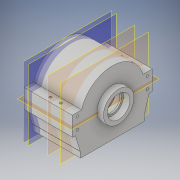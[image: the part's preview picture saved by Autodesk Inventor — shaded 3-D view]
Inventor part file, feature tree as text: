
AUTODESK INVENTOR PART (.ipt)
format: ipt  version: 2019 (Build 230136000, 136)  size: 587,776 bytes
history: native  units: mm
features: sketch x28, extrude x21, mirror x13, plane x12, projected_geometry x11, fillet x4, hole x3, other x1
ambient origin geometry x8: Origin, YZ Plane, XZ Plane, XY Plane, X Axis, Y Axis, Z Axis, Center Point
bodies: Body1 (feature_tree)
feature tree (93):
  other  "實體1"
  extrude  "擠出1"  Depth=123.43mm
  plane  "工作平面2"
  extrude  "擠出3"  Depth=160.0mm
  plane  "工作平面3"
  sketch  "草圖5"
  extrude  "擠出4"  Depth=120.0mm TaperAngle=0.0deg
  extrude  "擠出5"  [1 undecoded]
  plane  "工作平面4"
  extrude  "擠出7"  Depth=130.0mm
  plane  "工作平面5"
  extrude  "擠出9"  Depth=15.0mm TaperAngle=0.0deg
  extrude  "擠出10"  [1 undecoded]
  extrude  "擠出11"  Depth=140.0mm
  extrude  "擠出12"  Depth=10.0mm TaperAngle=0.0deg
  mirror  "鏡射1"
  fillet  "圓角2"  Radius=10.0mm
  fillet  "圓角3"  Radius=10.0mm
  sketch  "草圖16"
  plane  "工作平面7"
  mirror  "鏡射2"
  fillet  "圓角5"  [1 undecoded]
  fillet  "圓角6"  Radius=10.0mm
  plane  "工作平面8"
  plane  "工作平面9"
  sketch  "草圖20"
  sketch  "草圖21"
  extrude  "擠出15"  [1 undecoded]
  plane  "工作平面10"
  extrude  "擠出16"  Depth=10.0mm
  extrude  "擠出17"  Depth=10.0mm TaperAngle=0.0deg
  plane  "工作平面11"
  extrude  "擠出19"  Depth=10.0mm TaperAngle=0.0deg
  extrude  "擠出20"  Depth=160.0mm
  mirror  "鏡射3"
  mirror  "鏡射4"
  extrude  "擠出21"  Depth=80.0mm
  mirror  "鏡射7"
  plane  "工作平面15"
  mirror  "鏡射9"
  hole  "孔2"  [1 undecoded]
  mirror  "鏡射10"
  mirror  "鏡射11"
  hole  "孔3"  [1 undecoded]
  mirror  "鏡射12"
  mirror  "鏡射13"
  extrude  "擠出22"  Depth=160.0mm
  extrude  "擠出23"  Depth=120.0mm TaperAngle=0.0deg
  extrude  "擠出24"  Depth=120.0mm TaperAngle=0.0deg
  extrude  "擠出25"  Depth=25.0mm
  extrude  "擠出27"  Depth=20.0mm
  extrude  "擠出28"  Depth=2.0mm
  mirror  "鏡射14"
  plane  "工作平面17"
  hole  "孔4"  [1 undecoded]
  mirror  "鏡射15"
  mirror  "鏡射16"
  sketch  "草圖1"
  sketch  "草圖4"
  sketch  "草圖6"
  sketch  "草圖7"
  projected_geometry  "投影迴路1"
  sketch  "草圖9"
  projected_geometry  "投影迴路4"
  sketch  "草圖11"
  sketch  "草圖12"
  projected_geometry  "投影迴路6"
  sketch  "草圖13"
  projected_geometry  "投影迴路7"
  sketch  "草圖14"
  plane  "工作平面6"
  sketch  "草圖17"
  projected_geometry  "投影迴路8"
  sketch  "草圖24"
  projected_geometry  "投影迴路11"
  sketch  "草圖25"
  sketch  "草圖26"
  sketch  "草圖27"
  sketch  "草圖28"
  sketch  "草圖29"
  projected_geometry  "投影迴路12"
  sketch  "草圖30"
  sketch  "草圖31"
  sketch  "草圖32"
  projected_geometry  "投影迴路13"
  projected_geometry  "投影迴路14"
  projected_geometry  "投影迴路15"
  sketch  "草圖33"
  sketch  "草圖34"
  sketch  "草圖35"
  projected_geometry  "投影迴路16"
  sketch  "草圖36"
  sketch  "草圖37"
note: 7 required parameter values undecoded (feature->parameter linkage not recoverable at this tier; creation-order binding heuristic only, values carry confidence <= 0.55)
